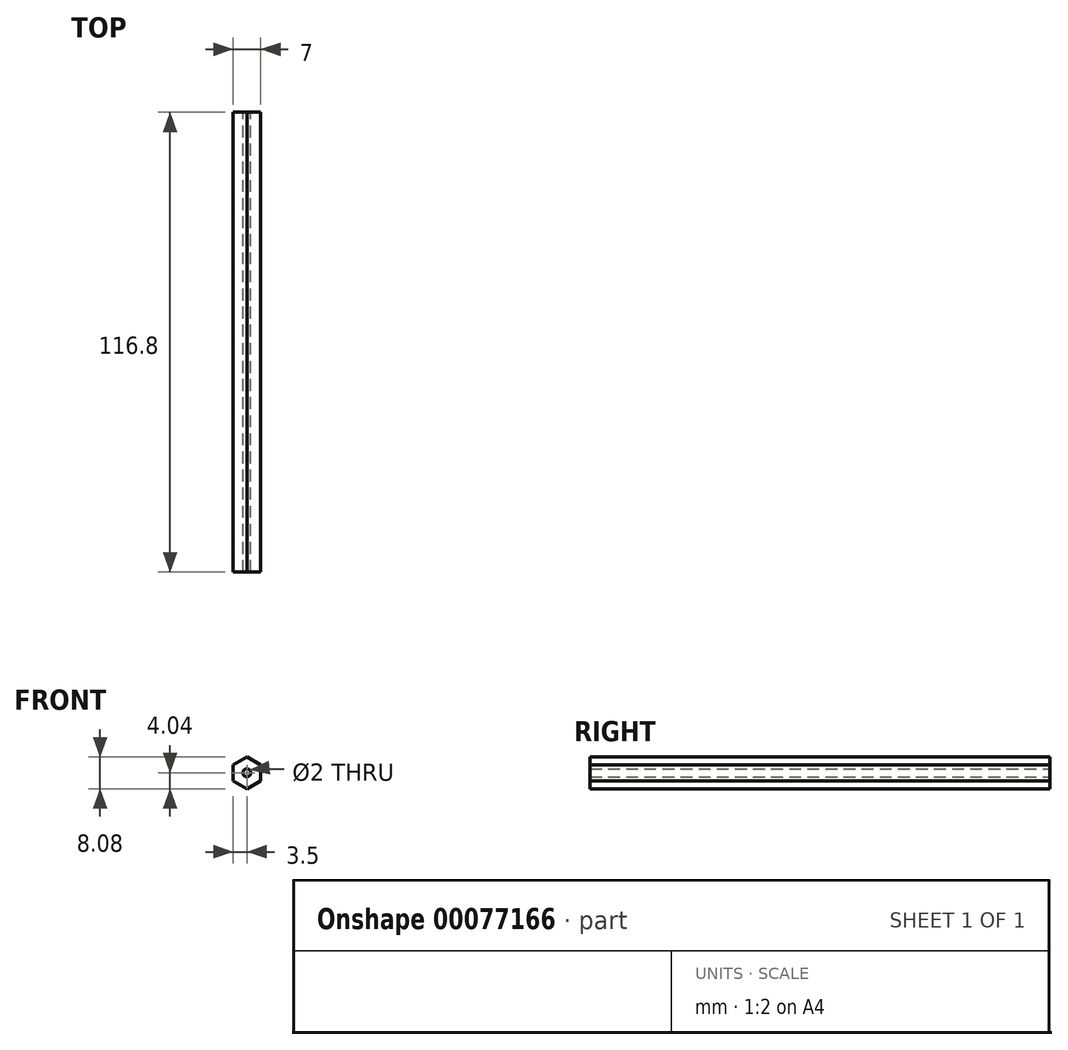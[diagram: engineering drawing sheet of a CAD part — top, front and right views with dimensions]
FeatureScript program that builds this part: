
annotation { "Feature Type Name" : "Feature", "Feature Type Description" : "" }
export const myFeature = defineFeature(function(context is Context, id is Id, definition is map)
    precondition{}
    {
        {
            var Q0;
            Q0=qCreatedBy(makeId("Front.planeOp"),FACE);
            var sketch = newSketch(context, id + "F0", { "sketchPlane" : qUnion([Q0])});
            skCircle(sketch, "E0.cCircle", {"center": v(0, 0) * mm, "radius": 3.5 * mm, "construction": true});
            skLineSegment(sketch, "E0.0", {"start": v(-3.5, -2.02) * mm, "end": v(-3.5, 2.02) * mm});
            skLineSegment(sketch, "E0.1", {"start": v(-3.5, 2.02) * mm, "end": v(0, 4.04) * mm});
            skLineSegment(sketch, "E0.2", {"start": v(0, 4.04) * mm, "end": v(3.5, 2.02) * mm});
            skLineSegment(sketch, "E0.3", {"start": v(3.5, 2.02) * mm, "end": v(3.5, -2.02) * mm});
            skLineSegment(sketch, "E0.4", {"start": v(3.5, -2.02) * mm, "end": v(0, -4.04) * mm});
            skLineSegment(sketch, "E0.5", {"start": v(0, -4.04) * mm, "end": v(-3.5, -2.02) * mm});
            skPoint(sketch, "E0.0.midPoint", {"position": v(-3.5, 0) * mm});
            skSolve(sketch);
        }
        {
            var Q0;
            Q0=qCreatedBy(makeId("Front.planeOp"),FACE);
            var sketch = newSketch(context, id + "F1", { "sketchPlane" : qUnion([Q0])});
            skPoint(sketch, "E1", {"position": v(0, 0) * mm});
            skSolve(sketch);
        }
        {
            var Q0;
            Q0=makeQuery(id+"F0.imprint","IMPRINT",FACE,{"disambiguationData":[TD([[makeQuery(id+"F0.imprint","IMPRINT",EDGE,{"derivedFrom":sQuery(id+"F0.wireOp",EDGE,"E0.0")}),-1.0]])]});
            extrude(context, id + "F2", {"entities" : qUnion([Q0]), "depth" : 150 * mm});
        }
        {
            var Q0;
            Q0=sQuery(id+"F1.wireOp",VERTEX,"E1");
            var Q1;
            Q1=makeQuery(id+"F2.opExtrude","SWEPT_BODY",BODY,{"disambiguationData":[OSD([sQuery(id+"F0.wireOp",EDGE,"E0.0"),sQuery(id+"F0.wireOp",EDGE,"E0.1"),sQuery(id+"F0.wireOp",EDGE,"E0.2"),sQuery(id+"F0.wireOp",EDGE,"E0.3"),sQuery(id+"F0.wireOp",EDGE,"E0.4"),sQuery(id+"F0.wireOp",EDGE,"E0.5")])]});
            hole(context, id + "F3", {"style" : HoleStyle.SIMPLE, "endStyle" : HoleEndStyle.THROUGH, "oppositeDirection" : true, "holeDiameter" : 2 * mm, "locations" : qUnion([Q0]), "scope" : qUnion([Q1]), "isTappedThrough" : true});
        }
        {
            var Q0;
            Q0=qCreatedBy(makeId("Front.planeOp"),FACE);
            var sketch = newSketch(context, id + "F4", { "sketchPlane" : qUnion([Q0])});
            skCircle(sketch, "E2", {"center": v(0, 0) * mm, "radius": 1 * mm});
            skSolve(sketch);
        }
        {
            var Q0;
            Q0=makeQuery(id+"F4.imprint","IMPRINT",FACE,{"disambiguationData":[TD([[makeQuery(id+"F4.imprint","IMPRINT",EDGE,{"derivedFrom":sQuery(id+"F4.wireOp",EDGE,"E2")}),1.0]])]});
            extrude(context, id + "F5", {"entities" : qUnion([Q0]), "depth" : 150 * mm});
        }
        {
            var Q0;
            Q0=qCreatedBy(makeId("Right.planeOp"),FACE);
            var sketch = newSketch(context, id + "F6", { "sketchPlane" : qUnion([Q0])});
            skLineSegment(sketch, "E3", {"start": v(0, -4.1) * mm, "end": v(-12, -4.1) * mm});
            skLineSegment(sketch, "E4", {"start": v(0, -4.1) * mm, "end": v(0, 0) * mm});
            skLineSegment(sketch, "E5", {"start": v(0, 0) * mm, "end": v(-12, -4.1) * mm});
            skSolve(sketch);
        }
        {
            var Q0;
            Q0=qCreatedBy(makeId("Top.planeOp"),FACE);
            var sketch = newSketch(context, id + "F7", { "sketchPlane" : qUnion([Q0])});
            skLineSegment(sketch, "E6", {"start": v(0, 4.09) * mm, "end": v(0, 1.16) * mm});
            skSolve(sketch);
        }
        {
            var Q0;
            Q0 = qSketchRegion(id + "F6", true);
            var Q1;
            Q1=sQuery(id+"F7.wireOp",EDGE,"E6");
            revolve(context, id + "F8", {"operationType" : NewBodyOperationType.REMOVE, "entities" : qUnion([Q0]), "axis" : qUnion([Q1]), "revolveType" : RevolveType.FULL, "oppositeDirection" : true});
        }
        {
            var Q0;
            Q0=qCreatedBy(makeId("Front.planeOp"),FACE);
            var sketch = newSketch(context, id + "F9", { "sketchPlane" : qUnion([Q0])});
            skCircle(sketch, "E7", {"center": v(0, 0) * mm, "radius": 4.79 * mm});
            skSolve(sketch);
        }
        {
            var Q0;
            Q0 = qSketchRegion(id + "F9", true);
            extrude(context, id + "F10", {"entities" : qUnion([Q0]), "depth" : 35 * mm});
        }
        {
            var Q0;
            Q0=qCreatedBy(makeId("Front.planeOp"),FACE);
            var sketch = newSketch(context, id + "F11", { "sketchPlane" : qUnion([Q0])});
            skCircle(sketch, "E8.cCircle", {"center": v(0, 0) * mm, "radius": 3.6 * mm, "construction": true});
            skLineSegment(sketch, "E8.0", {"start": v(0.03, 4.16) * mm, "end": v(3.61, 2.05) * mm});
            skLineSegment(sketch, "E8.1", {"start": v(3.61, 2.05) * mm, "end": v(3.59, -2.1) * mm});
            skLineSegment(sketch, "E8.2", {"start": v(3.59, -2.1) * mm, "end": v(-0.03, -4.16) * mm});
            skLineSegment(sketch, "E8.3", {"start": v(-0.03, -4.16) * mm, "end": v(-3.61, -2.05) * mm});
            skLineSegment(sketch, "E8.4", {"start": v(-3.61, -2.05) * mm, "end": v(-3.59, 2.1) * mm});
            skLineSegment(sketch, "E8.5", {"start": v(-3.59, 2.1) * mm, "end": v(0.03, 4.16) * mm});
            skPoint(sketch, "E8.0.midPoint", {"position": v(1.82, 3.1) * mm});
            skSolve(sketch);
        }
        {
            var Q0;
            Q0=makeQuery(id+"F11.imprint","IMPRINT",FACE,{"disambiguationData":[TD([[makeQuery(id+"F11.imprint","IMPRINT",EDGE,{"derivedFrom":sQuery(id+"F11.wireOp",EDGE,"E8.0")}),-1.0]])]});
            extrude(context, id + "F12", {"entities" : qUnion([Q0]), "operationType" : NewBodyOperationType.REMOVE, "depth" : 33.2 * mm});
        }
        {
            var Q0;
            Q0=makeQuery(id+"F10.opExtrude","SWEPT_BODY",BODY,{"disambiguationData":[OSD([sQuery(id+"F9.wireOp",EDGE,"E7")])]});
            transform(context, id + "F13", {"entities" : qUnion([Q0]), "transformType" : TransformType.TRANSLATION_3D, "dx" : 0 * mm, "dy" : -117 * mm, "dz" : 0 * mm, "makeCopy" : false});
        }
        {
            var Q0;
            Q0=qCreatedBy(makeId("Right.planeOp"),FACE);
            var sketch = newSketch(context, id + "F14", { "sketchPlane" : qUnion([Q0])});
            skFitSpline(sketch, "E9", {"points": [v(-151.97, 4.81) * mm, v(-171.94, -10.3) * mm, v(-192.7, 4.81) * mm], "startDerivative": vector(-0.15, -39.07) * mm, "endDerivative": vector(-0.53, 28.7) * mm});
            skLineSegment(sketch, "E10", {"start": v(-151.97, 4.81) * mm, "end": v(-192.7, 4.81) * mm});
            skSolve(sketch);
        }
        {
            var Q0;
            Q0=qCreatedBy(makeId("Right.planeOp"),FACE);
            var sketch = newSketch(context, id + "F15", { "sketchPlane" : qUnion([Q0])});
            skLineSegment(sketch, "E11", {"start": v(-152.65, 4.82) * mm, "end": v(-165.4, 4.82) * mm});
            skSolve(sketch);
        }
        {
            var Q0;
            Q0=makeQuery(id+"F14.imprint","IMPRINT",FACE,{"disambiguationData":[TD([[makeQuery(id+"F14.imprint","IMPRINT",EDGE,{"derivedFrom":sQuery(id+"F14.wireOp",EDGE,"E9")}),-1.0]])]});
            var Q1;
            Q1=sQuery(id+"F15.wireOp",EDGE,"E11");
            revolve(context, id + "F16", {"operationType" : NewBodyOperationType.ADD, "entities" : qUnion([Q0]), "axis" : qUnion([Q1]), "revolveType" : RevolveType.FULL});
        }
        {
            var Q0;
            Q0=qCreatedBy(makeId("Right.planeOp"),FACE);
            var sketch = newSketch(context, id + "F17", { "sketchPlane" : qUnion([Q0])});
            skFitSpline(sketch, "E12", {"points": [v(-152.6, 5.28) * mm, v(-171.22, -9.23) * mm, v(-191.98, 5.28) * mm], "startDerivative": vector(-0.34, -32.24) * mm, "endDerivative": vector(-0.53, 28.7) * mm});
            skLineSegment(sketch, "E13", {"start": v(-152.6, 5.28) * mm, "end": v(-191.98, 5.28) * mm});
            skSolve(sketch);
        }
        {
            var Q0;
            Q0=qCreatedBy(makeId("Right.planeOp"),FACE);
            var sketch = newSketch(context, id + "F18", { "sketchPlane" : qUnion([Q0])});
            skFitSpline(sketch, "E14", {"points": [v(-152, -4.79) * mm, v(-155.2, -4.96) * mm, v(-159.41, -6.21) * mm], "startDerivative": vector(-1.11, 0) * mm, "endDerivative": vector(-0.7, -0.56) * mm});
            skLineSegment(sketch, "E15", {"start": v(-159.4, -6.2) * mm, "end": v(-159.4, 0) * mm});
            skLineSegment(sketch, "E16", {"start": v(-159.4, 0) * mm, "end": v(-152, 0) * mm});
            skLineSegment(sketch, "E17", {"start": v(-152, 0) * mm, "end": v(-152, -4.79) * mm});
            skSolve(sketch);
        }
        {
            var Q0;
            Q0 = qSketchRegion(id + "F18", true);
            var Q1;
            Q1 = qSketchRegion(id + "F21", true);
            var Q2;
            Q2=sQuery(id+"F18.wireOp",EDGE,"E16");
            revolve(context, id + "F19", {"operationType" : NewBodyOperationType.ADD, "entities" : qUnion([Q0, Q1]), "axis" : qUnion([Q2]), "revolveType" : RevolveType.FULL});
        }
        {
            var Q0;
            Q0=makeQuery(id+"F17.imprint","IMPRINT",FACE,{"disambiguationData":[TD([[makeQuery(id+"F17.imprint","IMPRINT",EDGE,{"derivedFrom":sQuery(id+"F17.wireOp",EDGE,"E12")}),-1.0]])]});
            var Q1;
            Q1 = qSketchRegion(id + "F15", true);
            var Q2;
            Q2=sQuery(id+"F17.wireOp",EDGE,"E13");
            revolve(context, id + "F20", {"operationType" : NewBodyOperationType.REMOVE, "entities" : qUnion([Q0, Q1]), "axis" : qUnion([Q2]), "revolveType" : RevolveType.FULL, "oppositeDirection" : true});
        }
        {
            var Q0;
            Q0=qCreatedBy(makeId("Right.planeOp"),FACE);
            var sketch = newSketch(context, id + "F21", { "sketchPlane" : qUnion([Q0])});
            skLineSegment(sketch, "E18.bottom", {"start": v(-192.71, 4.79) * mm, "end": v(-149.92, 4.79) * mm});
            skLineSegment(sketch, "E18.top", {"start": v(-192.71, 20.55) * mm, "end": v(-149.92, 20.55) * mm});
            skLineSegment(sketch, "E18.left", {"start": v(-192.71, 4.79) * mm, "end": v(-192.71, 20.55) * mm});
            skLineSegment(sketch, "E18.right", {"start": v(-149.92, 4.79) * mm, "end": v(-149.92, 20.55) * mm});
            skSolve(sketch);
        }
        {
            var Q0;
            Q0=makeQuery(id+"F21.imprint","IMPRINT",FACE,{"disambiguationData":[TD([[makeQuery(id+"F21.imprint","IMPRINT",EDGE,{"derivedFrom":sQuery(id+"F21.wireOp",EDGE,"E18.bottom")}),1.0]])]});
            extrude(context, id + "F22", {"entities" : qUnion([Q0]), "operationType" : NewBodyOperationType.REMOVE, "oppositeDirection" : true, "depth" : 50 * mm, "hasSecondDirection" : true, "secondDirectionOppositeDirection" : false, "secondDirectionDepth" : 47.52 * mm});
        }
    });
